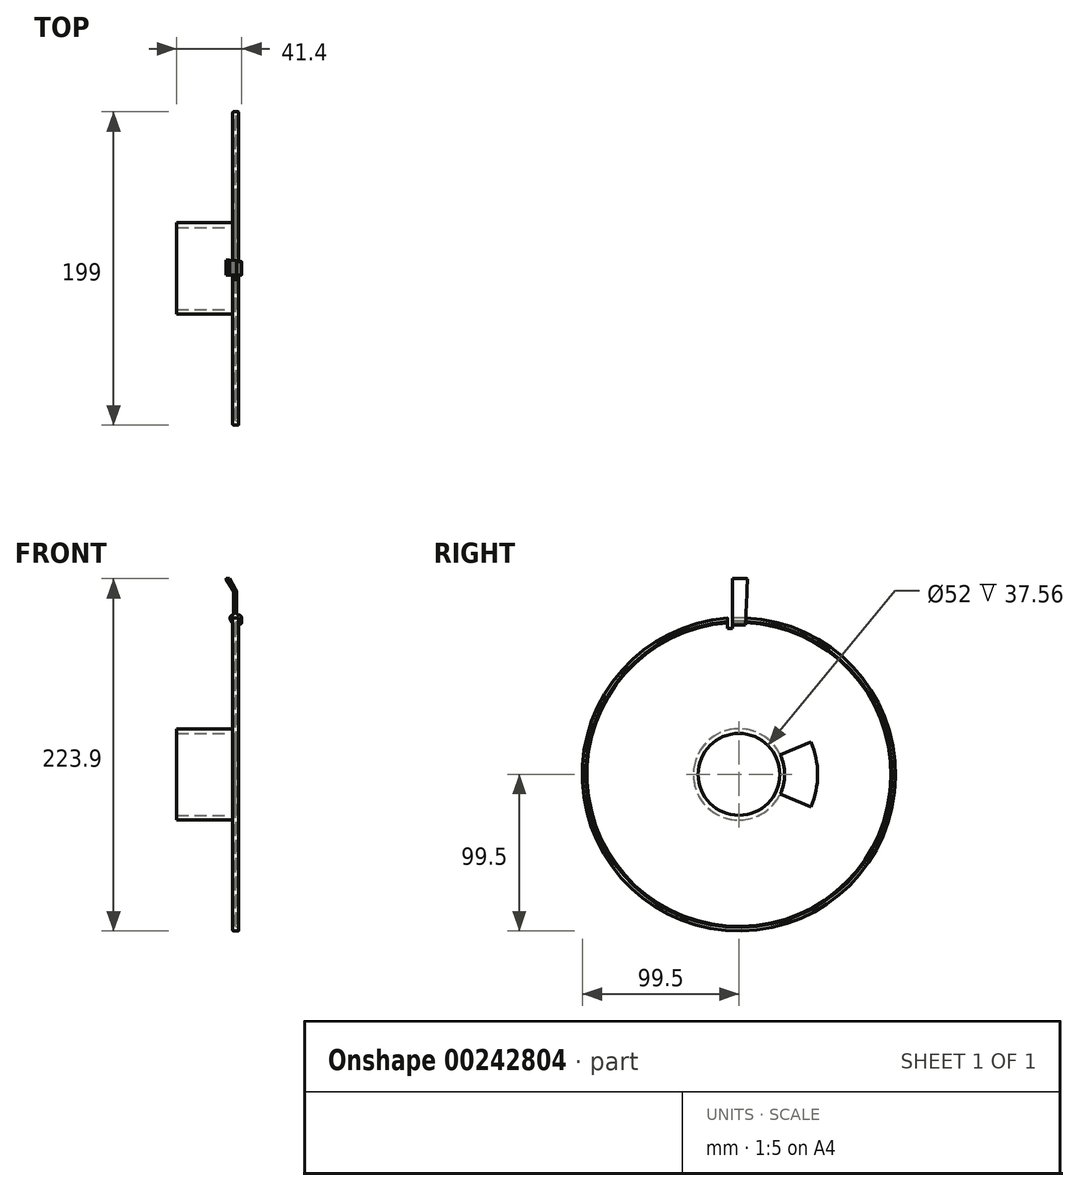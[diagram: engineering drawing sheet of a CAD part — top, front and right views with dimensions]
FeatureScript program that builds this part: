
annotation { "Feature Type Name" : "Feature", "Feature Type Description" : "" }
export const myFeature = defineFeature(function(context is Context, id is Id, definition is map)
    precondition{}
    {
        {
            var Q0;
            Q0=qCreatedBy(makeId("Front.planeOp"),FACE);
            var sketch = newSketch(context, id + "F0", { "sketchPlane" : qUnion([Q0])});
            skLineSegment(sketch, "E0", {"start": v(0, 0) * mm, "end": v(0, 29) * mm});
            skLineSegment(sketch, "E1.MirrorCS", {"start": v(36.2, 99.5) * mm, "end": v(39, 99.5) * mm});
            skLineSegment(sketch, "E2.MirrorCS", {"start": v(35.7, 29) * mm, "end": v(35.7, 99) * mm});
            skLineSegment(sketch, "E3.MirrorCS", {"start": v(0, 29) * mm, "end": v(35.7, 29) * mm});
            skLineSegment(sketch, "E4", {"start": v(39.5, 99) * mm, "end": v(39.5, 97.3) * mm});
            skLineSegment(sketch, "E5", {"start": v(37.56, 96.6) * mm, "end": v(37.56, 26) * mm});
            skLineSegment(sketch, "E6", {"start": v(50.4, 0) * mm, "end": v(-44.5, 0) * mm, "construction": true});
            skLineSegment(sketch, "E7", {"start": v(37.56, 26) * mm, "end": v(0, 26) * mm});
            skPoint(sketch, "E8.visualSharp", {"position": v(39.5, 99.5) * mm});
            skArc(sketch, "E8.filletArc", {"start": v(39.5, 99) * mm, "mid": v(39.35, 99.35) * mm, "end": v(39, 99.5) * mm});
            skPoint(sketch, "E9.visualSharp", {"position": v(35.7, 99.5) * mm});
            skArc(sketch, "E9.filletArc", {"start": v(36.2, 99.5) * mm, "mid": v(35.85, 99.35) * mm, "end": v(35.7, 99) * mm});
            skLineSegment(sketch, "E10", {"start": v(39.5, 97.3) * mm, "end": v(37.56, 96.6) * mm});
            skArc(sketch, "E11.MirrorCS", {"start": v(-36.2, 99.5) * mm, "mid": v(-35.85, 99.35) * mm, "end": v(-35.7, 99) * mm});
            skArc(sketch, "E12.MirrorCS", {"start": v(-39.5, 99) * mm, "mid": v(-39.35, 99.35) * mm, "end": v(-39, 99.5) * mm});
            skLineSegment(sketch, "E13.MirrorCS", {"start": v(-36.2, 99.5) * mm, "end": v(-39, 99.5) * mm});
            skLineSegment(sketch, "E14.MirrorCS", {"start": v(-39.5, 97.3) * mm, "end": v(-37.56, 96.6) * mm});
            skLineSegment(sketch, "E15.MirrorCS", {"start": v(-39.5, 99) * mm, "end": v(-39.5, 97.3) * mm});
            skPoint(sketch, "E16.MirrorP", {"position": v(-35.7, 99.5) * mm});
            skLineSegment(sketch, "E17.MirrorCS", {"start": v(-37.56, 96.6) * mm, "end": v(-37.56, 26) * mm});
            skPoint(sketch, "E18.MirrorP", {"position": v(-39.5, 99.5) * mm});
            skLineSegment(sketch, "E19.MirrorCS", {"start": v(0, 29) * mm, "end": v(-35.7, 29) * mm});
            skLineSegment(sketch, "E20.MirrorCS", {"start": v(-37.56, 26) * mm, "end": v(0, 26) * mm});
            skLineSegment(sketch, "E21.MirrorCS", {"start": v(-35.7, 29) * mm, "end": v(-35.7, 99) * mm});
            skLineSegment(sketch, "E22.0", {"start": v(39.4, 97.37) * mm, "end": v(38.56, 97.07) * mm});
            skArc(sketch, "E22.1", {"start": v(36.2, 99.4) * mm, "mid": v(35.92, 99.28) * mm, "end": v(35.8, 99) * mm});
            skLineSegment(sketch, "E22.2", {"start": v(36.2, 99.4) * mm, "end": v(39, 99.4) * mm});
            skArc(sketch, "E22.3", {"start": v(39.4, 99) * mm, "mid": v(39.28, 99.28) * mm, "end": v(39, 99.4) * mm});
            skLineSegment(sketch, "E22.4", {"start": v(39.4, 99) * mm, "end": v(39.4, 97.37) * mm});
            skLineSegment(sketch, "E23.0", {"start": v(41.4, 95.97) * mm, "end": v(38.56, 94.94) * mm});
            skArc(sketch, "E23.1", {"start": v(36.2, 101.4) * mm, "mid": v(34.5, 100.7) * mm, "end": v(33.8, 99) * mm});
            skLineSegment(sketch, "E23.2", {"start": v(36.2, 101.4) * mm, "end": v(39, 101.4) * mm});
            skArc(sketch, "E23.3", {"start": v(41.4, 99) * mm, "mid": v(40.7, 100.7) * mm, "end": v(39, 101.4) * mm});
            skLineSegment(sketch, "E23.4", {"start": v(41.4, 99) * mm, "end": v(41.4, 95.97) * mm});
            skLineSegment(sketch, "E24", {"start": v(38.56, 97.07) * mm, "end": v(38.56, 94.94) * mm});
            skLineSegment(sketch, "E25", {"start": v(35.8, 99) * mm, "end": v(35.8, 96.7) * mm});
            skLineSegment(sketch, "E26", {"start": v(36.2, 101.4) * mm, "end": v(36.2, 116.4) * mm});
            skLineSegment(sketch, "E27", {"start": v(36.2, 116.4) * mm, "end": v(38.2, 116.4) * mm});
            skLineSegment(sketch, "E28", {"start": v(38.2, 116.4) * mm, "end": v(38.2, 101.4) * mm});
            skLineSegment(sketch, "E29", {"start": v(33.58, 124.4) * mm, "end": v(31.58, 124.4) * mm});
            skLineSegment(sketch, "E30", {"start": v(33.58, 124.4) * mm, "end": v(38.2, 116.4) * mm});
            skLineSegment(sketch, "E31", {"start": v(31.58, 124.4) * mm, "end": v(36.2, 116.4) * mm});
            skLineSegment(sketch, "E32", {"start": v(35.6, 96.5) * mm, "end": v(35.41, 96.5) * mm});
            skLineSegment(sketch, "E33", {"start": v(35.24, 96.6) * mm, "end": v(33.8, 99) * mm});
            skPoint(sketch, "E34.visualSharp", {"position": v(35.8, 96.5) * mm});
            skArc(sketch, "E34.filletArc", {"start": v(35.6, 96.5) * mm, "mid": v(35.74, 96.56) * mm, "end": v(35.8, 96.7) * mm});
            skPoint(sketch, "E35.visualSharp", {"position": v(35.3, 96.5) * mm});
            skArc(sketch, "E35.filletArc", {"start": v(35.24, 96.6) * mm, "mid": v(35.31, 96.53) * mm, "end": v(35.41, 96.5) * mm});
            skSolve(sketch);
        }
        {
            var Q0;
            {var subQ6=sQuery(id+"F0.wireOp",EDGE,"E3.MirrorCS");Q0=makeQuery(id+"F0.imprint","IMPRINT",FACE,{"disambiguationData":[TD([[makeQuery(id+"F0.imprint","IMPRINT",EDGE,{"derivedFrom":subQ6}),-1.0]])]});}
            var Q1;
            Q1=makeQuery(id+"F0.imprint","IMPRINT",FACE,{"disambiguationData":[TD([[makeQuery(id+"F0.imprint","IMPRINT",EDGE,{"derivedFrom":sQuery(id+"F0.wireOp",EDGE,"E1.MirrorCS")}),-1.0]])]});
            var Q2;
            Q2=makeQuery(id+"F0.imprint","IMPRINT",FACE,{"disambiguationData":[TD([[makeQuery(id+"F0.imprint","IMPRINT",EDGE,{"derivedFrom":sQuery(id+"F0.wireOp",EDGE,"E11.MirrorCS")}),-1.0]])]});
            var Q3;
            Q3=sQuery(id+"F0.wireOp",EDGE,"E6");
            revolve(context, id + "F1", {"entities" : qUnion([Q0, Q1, Q2]), "axis" : qUnion([Q3]), "revolveType" : RevolveType.FULL});
        }
        {
            var Q0;
            Q0=makeQuery(id+"F1.opRevolve","SWEPT_FACE",FACE,{"disambiguationData":[OSD([sQuery(id+"F0.wireOp",EDGE,"E5")])]});
            var sketch = newSketch(context, id + "F2", { "sketchPlane" : qUnion([Q0])});
            skLineSegment(sketch, "E36", {"start": v(0, 0) * mm, "end": v(46.69, 0) * mm, "construction": true});
            skLineSegment(sketch, "E37", {"start": v(45.58, 20.5) * mm, "end": v(26.17, 12.5) * mm});
            skLineSegment(sketch, "E38.MirrorCS", {"start": v(45.58, -20.5) * mm, "end": v(26.17, -12.5) * mm});
            skCircle(sketch, "E39", {"center": v(0, 0) * mm, "radius": 29 * mm});
            skArc(sketch, "E40", {"start": v(45.58, -20.5) * mm, "mid": v(49.98, 0) * mm, "end": v(45.58, 20.5) * mm});
            skSolve(sketch);
        }
        {
            var Q0;
            Q0=makeQuery(id+"F2.imprint","IMPRINT",FACE,{"disambiguationData":[TD([[makeQuery(id+"F2.imprint","IMPRINT",EDGE,{"derivedFrom":makeQuery(id+"F1.opRevolve","SWEPT_EDGE",EDGE,{"disambiguationData":[OSD([sQuery(id+"F0.wireOp",EDGE,"4677f349-bfd8-4fea-8fc9-91be8f14c4cf3.MirrorCS"),sQuery(id+"F0.wireOp",EDGE,"BIqN7IFA-w8t2-s2uV-94cp-YeS90QZtlOkr")])]})}),-1.0]])]});
            var Q1;
            {var subQ0=sQuery(id+"F2.wireOp",EDGE,"E37");Q1=makeQuery(id+"F2.imprint","IMPRINT",FACE,{"disambiguationData":[TD([[makeQuery(id+"F2.imprint","IMPRINT",EDGE,{"derivedFrom":subQ0}),1.0]])]});}
            extrude(context, id + "F3", {"entities" : qUnion([Q0, Q1]), "operationType" : NewBodyOperationType.REMOVE, "endBound" : BoundingType.THROUGH_ALL, "oppositeDirection" : true, "depth" : 25 * mm});
        }
        {
            var Q0;
            {var subQ0=sQuery(id+"F0.wireOp",EDGE,"E26");Q0=makeQuery(id+"F0.imprint","IMPRINT",FACE,{"disambiguationData":[TD([[makeQuery(id+"F0.imprint","IMPRINT",EDGE,{"derivedFrom":subQ0}),-1.0]])]});}
            var Q1;
            Q1=makeQuery(id+"F0.imprint","IMPRINT",FACE,{"disambiguationData":[TD([[makeQuery(id+"F0.imprint","IMPRINT",EDGE,{"derivedFrom":sQuery(id+"F0.wireOp",EDGE,"E27")}),1.0]])]});
            var Q2;
            Q2=makeQuery(id+"F0.imprint","IMPRINT",FACE,{"disambiguationData":[TD([[makeQuery(id+"F0.imprint","IMPRINT",EDGE,{"derivedFrom":sQuery(id+"F0.wireOp",EDGE,"E1.MirrorCS")}),1.0]])]});
            var Q3;
            Q3=makeQuery(id+"F0.imprint","IMPRINT",FACE,{"disambiguationData":[TD([[makeQuery(id+"F0.imprint","IMPRINT",EDGE,{"derivedFrom":sQuery(id+"F0.wireOp",EDGE,"E1.MirrorCS")}),-1.0]])]});
            var Q4;
            Q4=makeQuery(id+"F1.opRevolve","SWEPT_EDGE",EDGE,{"disambiguationData":[OSD([sQuery(id+"F0.wireOp",EDGE,"E5"),sQuery(id+"F0.wireOp",EDGE,"E7")])]});
            revolve(context, id + "F4", {"entities" : qUnion([Q0, Q1, Q2, Q3]), "axis" : qUnion([Q4]), "revolveType" : RevolveType.SYMMETRIC, "angle" : 5 * degree});
        }
        {
            var Q0;
            Q0=makeQuery(id+"F4.opRevolve","SWEPT_FACE",FACE,{"disambiguationData":[OSD([sQuery(id+"F0.wireOp",EDGE,"E23.4")])]});
            var sketch = newSketch(context, id + "F5", { "sketchPlane" : qUnion([Q0])});
            skArc(sketch, "E41.0.0", {"start": v(4.32, 98.9) * mm, "mid": v(0, 99) * mm, "end": v(-4.32, 98.9) * mm});
            skLineSegment(sketch, "E41.0.1", {"start": v(-4.32, 98.9) * mm, "end": v(-4.19, 95.87) * mm});
            skArc(sketch, "E41.0.2", {"start": v(-4.19, 95.87) * mm, "mid": v(0, 95.97) * mm, "end": v(4.19, 95.87) * mm});
            skLineSegment(sketch, "E41.0.3", {"start": v(4.19, 95.87) * mm, "end": v(4.32, 98.9) * mm});
            skLineSegment(sketch, "E42", {"start": v(-4.19, 95.87) * mm, "end": v(-4.19, 127.4) * mm});
            skLineSegment(sketch, "E43", {"start": v(-4.19, 127.4) * mm, "end": v(-7.19, 127.4) * mm});
            skLineSegment(sketch, "E44", {"start": v(-4.19, 95.87) * mm, "end": v(-4.19, 92.85) * mm});
            skLineSegment(sketch, "E45", {"start": v(-4.19, 92.85) * mm, "end": v(-7.19, 92.85) * mm});
            skLineSegment(sketch, "E46", {"start": v(-7.19, 127.4) * mm, "end": v(-7.19, 92.85) * mm});
            skSolve(sketch);
        }
        {
            var Q0;
            {var subQ4=sQuery(id+"F5.wireOp",EDGE,"E41.0.1");Q0=makeQuery(id+"F5.imprint","IMPRINT",FACE,{"disambiguationData":[TD([[makeQuery(id+"F5.imprint","IMPRINT",EDGE,{"derivedFrom":subQ4}),-1.0]])]});}
            var Q1;
            {var subQ0=sQuery(id+"F5.wireOp",EDGE,"E41.0.1");Q1=makeQuery(id+"F5.imprint","IMPRINT",FACE,{"disambiguationData":[TD([[makeQuery(id+"F5.imprint","IMPRINT",EDGE,{"derivedFrom":subQ0}),1.0]])]});}
            extrude(context, id + "F6", {"entities" : qUnion([Q0, Q1]), "operationType" : NewBodyOperationType.REMOVE, "endBound" : BoundingType.THROUGH_ALL, "oppositeDirection" : true, "depth" : 25 * mm});
        }
        {
            var Q0;
            Q0=makeQuery(id+"F4.opRevolve","SWEPT_EDGE",EDGE,{"disambiguationData":[OSD([sQuery(id+"F0.wireOp",EDGE,"E23.2"),sQuery(id+"F0.wireOp",EDGE,"E28")])]});
            var Q1;
            Q1=makeQuery(id+"F4.opRevolve","SWEPT_EDGE",EDGE,{"disambiguationData":[OSD([sQuery(id+"F0.wireOp",EDGE,"E23.1"),sQuery(id+"F0.wireOp",EDGE,"E23.2"),sQuery(id+"F0.wireOp",EDGE,"E26")])]});
            var Q2;
            Q2=makeQuery(id+"F4.opRevolve","SWEPT_EDGE",EDGE,{"disambiguationData":[OSD([sQuery(id+"F0.wireOp",EDGE,"E23.0"),sQuery(id+"F0.wireOp",EDGE,"E23.4")])]});
            var Q3;
            Q3=makeQuery(id+"F4.opRevolve","SWEPT_EDGE",EDGE,{"disambiguationData":[OSD([sQuery(id+"F0.wireOp",EDGE,"E23.1"),sQuery(id+"F0.wireOp",EDGE,"E33")])]});
            fillet(context, id + "F7", {"entities" : qUnion([Q0, Q1, Q2, Q3]), "radius" : 1 * mm, "tangentPropagation" : true, "allowEdgeOverflow" : false});
        }
        {
            var Q0;
            Q0=makeQuery(id+"F4.opRevolve","SWEPT_EDGE",EDGE,{"disambiguationData":[OSD([sQuery(id+"F0.wireOp",EDGE,"E27"),sQuery(id+"F0.wireOp",EDGE,"E28"),sQuery(id+"F0.wireOp",EDGE,"E30")])]});
            var Q1;
            Q1=makeQuery(id+"F4.opRevolve","SWEPT_EDGE",EDGE,{"disambiguationData":[OSD([sQuery(id+"F0.wireOp",EDGE,"E26"),sQuery(id+"F0.wireOp",EDGE,"E27"),sQuery(id+"F0.wireOp",EDGE,"E31")])]});
            fillet(context, id + "F8", {"entities" : qUnion([Q0, Q1]), "radius" : 5 * mm, "tangentPropagation" : true, "allowEdgeOverflow" : false});
        }
    });
